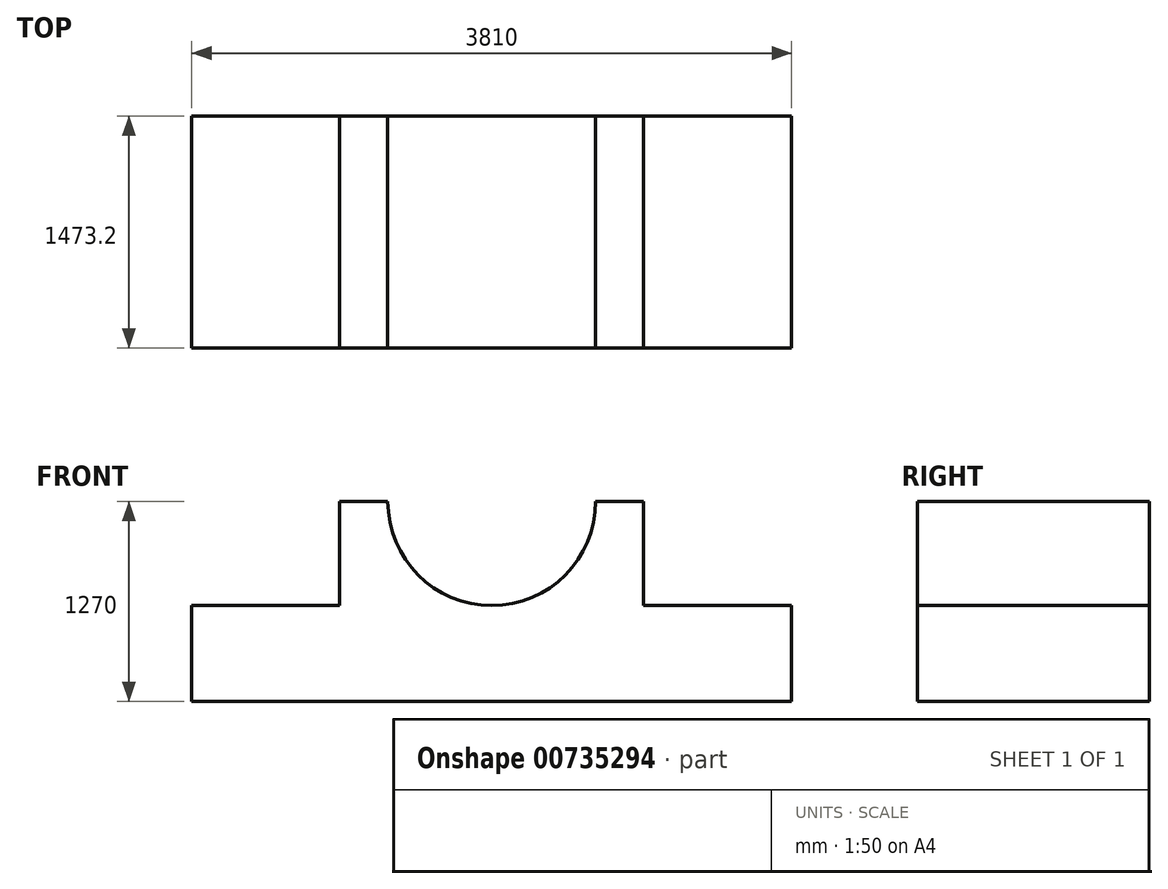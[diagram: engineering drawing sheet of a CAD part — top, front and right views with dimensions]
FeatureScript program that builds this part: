
annotation { "Feature Type Name" : "Feature", "Feature Type Description" : "" }
export const myFeature = defineFeature(function(context is Context, id is Id, definition is map)
    precondition{}
    {
        {
            var Q0;
            Q0=qCreatedBy(makeId("Front.planeOp"),FACE);
            var sketch = newSketch(context, id + "F0", { "sketchPlane" : qUnion([Q0])});
            skLineSegment(sketch, "E0.bottom", {"start": v(-1999.8, 1237.79) * mm, "end": v(-69.4, 1237.79) * mm});
            skLineSegment(sketch, "E0.top", {"start": v(-1999.8, -32.21) * mm, "end": v(-69.4, -32.21) * mm});
            skLineSegment(sketch, "E0.left", {"start": v(-1999.8, 1237.79) * mm, "end": v(-1999.8, -32.21) * mm});
            skLineSegment(sketch, "E0.right", {"start": v(-69.4, 1237.79) * mm, "end": v(-69.4, -32.21) * mm});
            skLineSegment(sketch, "E1.bottom", {"start": v(-2939.6, 577.39) * mm, "end": v(870.4, 577.39) * mm});
            skLineSegment(sketch, "E1.top", {"start": v(-2939.6, -32.21) * mm, "end": v(870.4, -32.21) * mm});
            skLineSegment(sketch, "E1.left", {"start": v(-2939.6, 577.39) * mm, "end": v(-2939.6, -32.21) * mm});
            skLineSegment(sketch, "E1.right", {"start": v(870.4, 577.39) * mm, "end": v(870.4, -32.21) * mm});
            skSolve(sketch);
        }
        {
            var Q0;
            {var subQ5=sQuery(id+"F0.wireOp",EDGE,"E1.right");Q0=makeQuery(id+"F0.imprint","IMPRINT",FACE,{"disambiguationData":[TD([[makeQuery(id+"F0.imprint","IMPRINT",EDGE,{"derivedFrom":subQ5}),-1.0]])]});}
            var Q1;
            {var subQ0=sQuery(id+"F0.wireOp",EDGE,"E1.top");var subQ1=sQuery(id+"F0.wireOp",EDGE,"E0.left");var subQ2=makeQuery(id+"F0.imprint","INTERSECT",VERTEX,{"derivedFrom":[subQ1,subQ0]});Q1=makeQuery(id+"F0.imprint","IMPRINT",FACE,{"disambiguationData":[TD([[makeQuery(id+"F0.imprint","IMPRINT",EDGE,{"disambiguationData":[TD([[subQ2,1.0]])],"derivedFrom":subQ1}),1.0]])]});}
            var Q2;
            {var subQ0=sQuery(id+"F0.wireOp",EDGE,"E0.bottom");Q2=makeQuery(id+"F0.imprint","IMPRINT",FACE,{"disambiguationData":[TD([[makeQuery(id+"F0.imprint","IMPRINT",EDGE,{"derivedFrom":subQ0}),-1.0]])]});}
            var Q3;
            {var subQ5=sQuery(id+"F0.wireOp",EDGE,"E1.left");Q3=makeQuery(id+"F0.imprint","IMPRINT",FACE,{"disambiguationData":[TD([[makeQuery(id+"F0.imprint","IMPRINT",EDGE,{"derivedFrom":subQ5}),1.0]])]});}
            extrude(context, id + "F1", {"entities" : qUnion([Q0, Q1, Q2, Q3]), "depth" : 1473.2 * mm, "offsetDistance" : 25.4 * mm});
        }
        {
            var Q0;
            Q0=makeQuery(id+"F1.opExtrude","CAP_FACE",FACE,{"disambiguationData":[OSD([sQuery(id+"F0.wireOp",EDGE,"E0.bottom"),sQuery(id+"F0.wireOp",EDGE,"E0.left"),sQuery(id+"F0.wireOp",EDGE,"E0.right"),sQuery(id+"F0.wireOp",EDGE,"E1.bottom"),sQuery(id+"F0.wireOp",EDGE,"E1.top"),sQuery(id+"F0.wireOp",EDGE,"E1.left"),sQuery(id+"F0.wireOp",EDGE,"E1.right")])],"isStart":false});
            var sketch = newSketch(context, id + "F2", { "sketchPlane" : qUnion([Q0])});
            skCircle(sketch, "E2", {"center": v(-1034.6, 1237.79) * mm, "radius": 660.4 * mm});
            skSolve(sketch);
        }
        {
            var Q0;
            {var subQ0=sQuery(id+"F2.wireOp",EDGE,"E2");var subQ1=makeQuery(id+"F1.opExtrude","CAP_EDGE",EDGE,{"disambiguationData":[OSD([sQuery(id+"F0.wireOp",EDGE,"E0.bottom")])],"isStart":false});var subQ2=makeQuery(id+"F2.imprint","INTERSECT",VERTEX,{"disambiguationData":[OD(0.0)],"derivedFrom":[subQ1,subQ0]});Q0=makeQuery(id+"F2.imprint","IMPRINT",FACE,{"disambiguationData":[TD([[makeQuery(id+"F2.imprint","IMPRINT",EDGE,{"disambiguationData":[TD([[subQ2,-1.0]])],"derivedFrom":subQ0}),1.0]])]});}
            extrude(context, id + "F3", {"entities" : qUnion([Q0]), "operationType" : NewBodyOperationType.REMOVE, "oppositeDirection" : true, "depth" : 1524 * mm, "offsetDistance" : 25.4 * mm});
        }
    });
